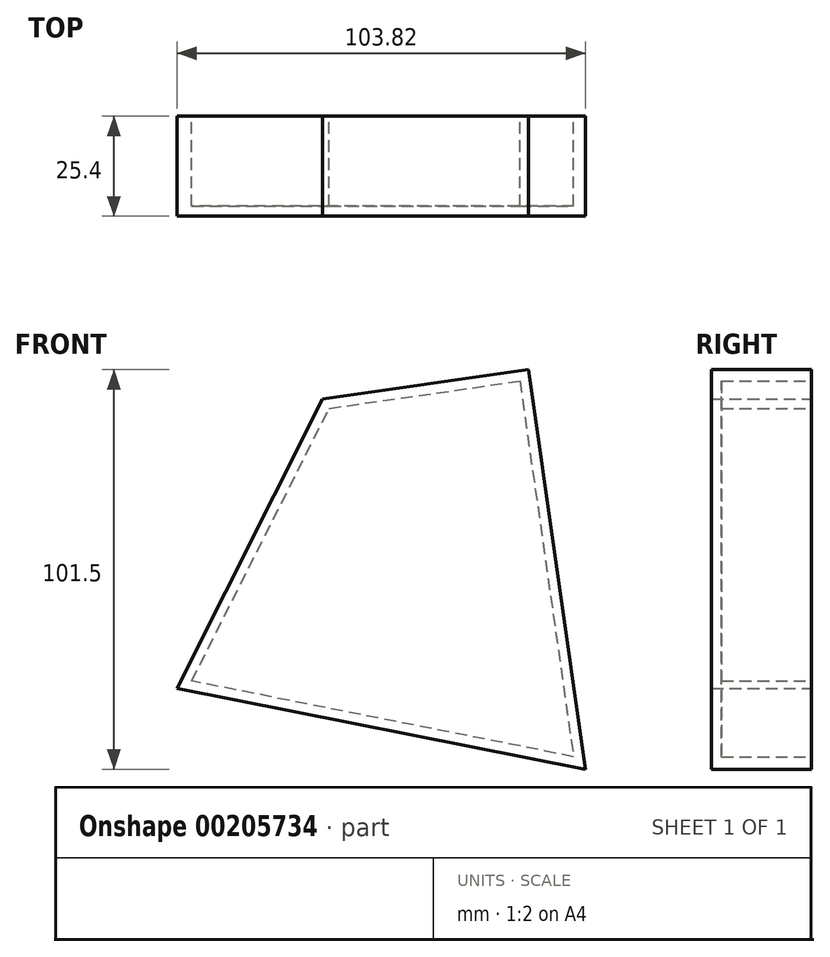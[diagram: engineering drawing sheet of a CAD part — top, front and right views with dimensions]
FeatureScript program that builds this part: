
annotation { "Feature Type Name" : "Feature", "Feature Type Description" : "" }
export const myFeature = defineFeature(function(context is Context, id is Id, definition is map)
    precondition{}
    {
        {
            var Q0;
            Q0=qCreatedBy(makeId("Front.planeOp"),FACE);
            var sketch = newSketch(context, id + "F0", { "sketchPlane" : qUnion([Q0])});
            skLineSegment(sketch, "E0", {"start": v(-15.32, 44.72) * mm, "end": v(36.93, 52.2) * mm});
            skLineSegment(sketch, "E1", {"start": v(36.93, 52.2) * mm, "end": v(51.46, -49.3) * mm});
            skLineSegment(sketch, "E2", {"start": v(51.46, -49.3) * mm, "end": v(-52.36, -28.76) * mm});
            skLineSegment(sketch, "E3", {"start": v(-52.36, -28.76) * mm, "end": v(-15.32, 44.72) * mm});
            skSolve(sketch);
        }
        {
            var Q0;
            Q0 = qSketchRegion(id + "F0", true);
            extrude(context, id + "F1", {"entities" : qUnion([Q0]), "depth" : 25.4 * mm});
        }
        {
            var Q0;
            Q0=makeQuery(id+"F1.opExtrude","CAP_FACE",FACE,{"disambiguationData":[OSD([sQuery(id+"F0.wireOp",EDGE,"E0"),sQuery(id+"F0.wireOp",EDGE,"E1"),sQuery(id+"F0.wireOp",EDGE,"E2"),sQuery(id+"F0.wireOp",EDGE,"E3")])],"isStart":true});
            shell(context, id + "F2", {"entities" : qUnion([Q0]), "thickness" : 2.54 * mm});
        }
    });
